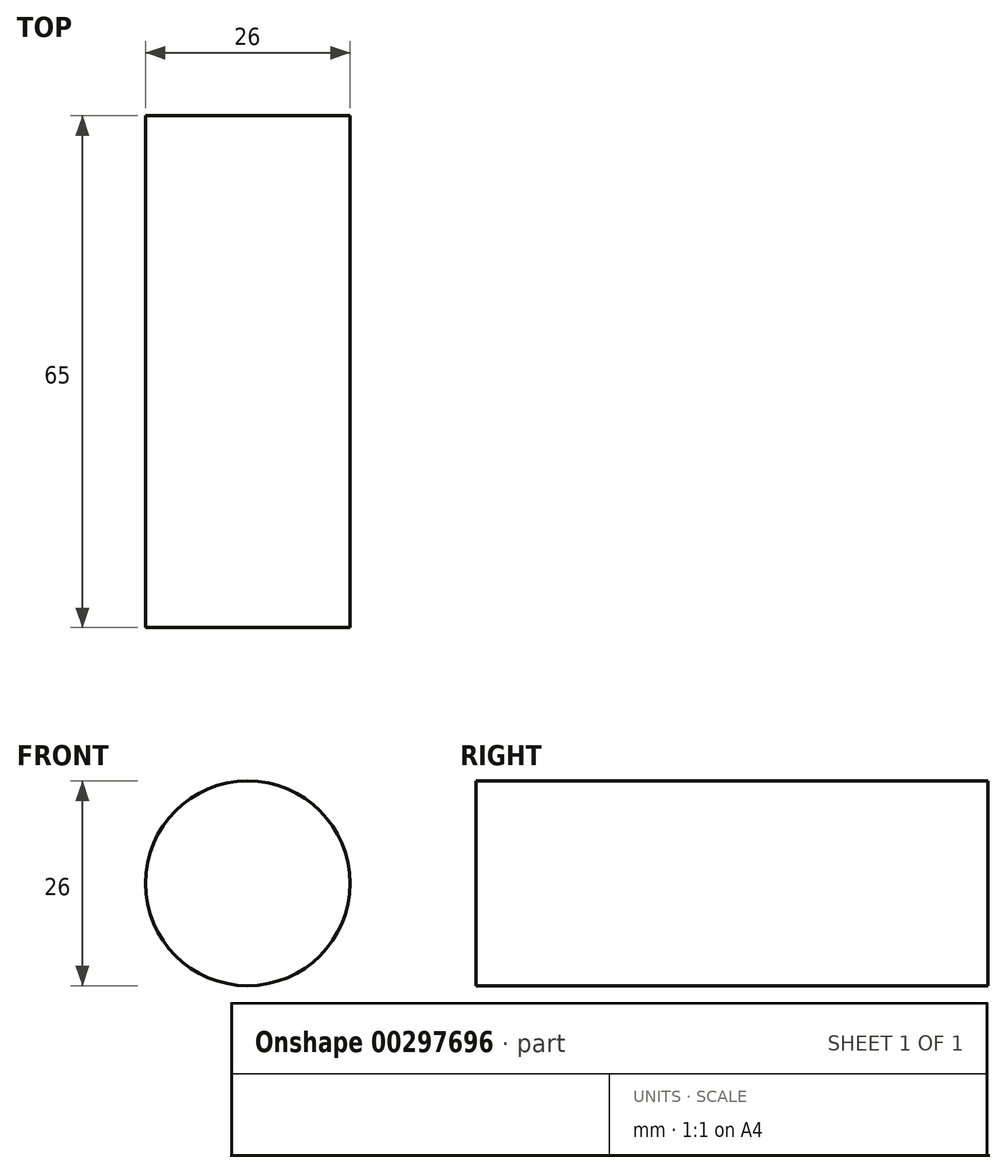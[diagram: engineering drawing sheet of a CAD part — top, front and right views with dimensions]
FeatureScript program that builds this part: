
annotation { "Feature Type Name" : "Feature", "Feature Type Description" : "" }
export const myFeature = defineFeature(function(context is Context, id is Id, definition is map)
    precondition{}
    {
        {
            var Q0;
            Q0=qCreatedBy(makeId("Front.planeOp"),FACE);
            var sketch = newSketch(context, id + "F0", { "sketchPlane" : qUnion([Q0])});
            skCircle(sketch, "E0", {"center": v(0, 0) * mm, "radius": 13 * mm});
            skSolve(sketch);
        }
        {
            var Q0;
            Q0=makeQuery(id+"F0.imprint","IMPRINT",FACE,{"disambiguationData":[TD([[makeQuery(id+"F0.imprint","IMPRINT",EDGE,{"derivedFrom":sQuery(id+"F0.wireOp",EDGE,"E0")}),1.0]])]});
            extrude(context, id + "F1", {"entities" : qUnion([Q0]), "depth" : 65 * mm});
        }
    });
